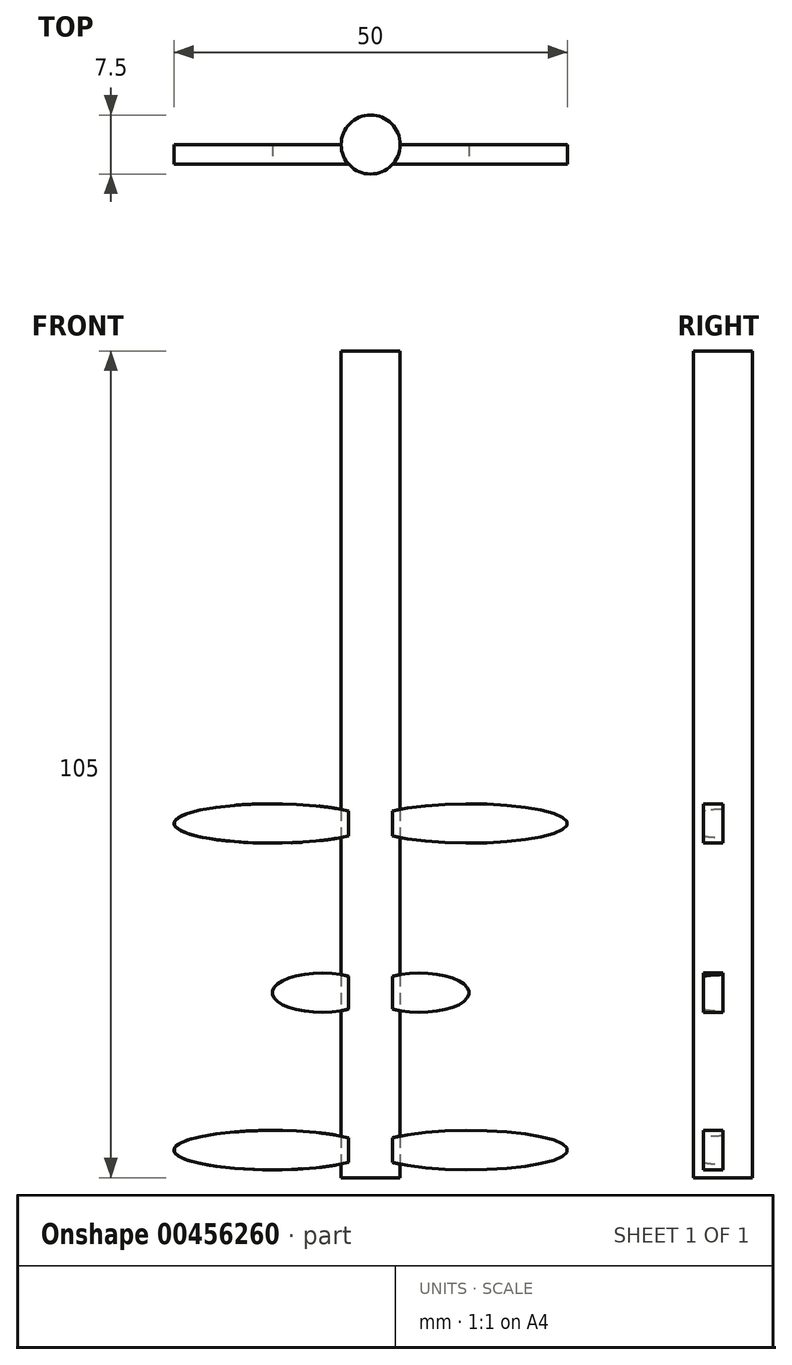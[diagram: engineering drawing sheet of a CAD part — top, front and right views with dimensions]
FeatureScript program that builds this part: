
annotation { "Feature Type Name" : "Feature", "Feature Type Description" : "" }
export const myFeature = defineFeature(function(context is Context, id is Id, definition is map)
    precondition{}
    {
        {
            var Q0;
            Q0=qCreatedBy(makeId("Top.planeOp"),FACE);
            var sketch = newSketch(context, id + "F0", { "sketchPlane" : qUnion([Q0])});
            skCircle(sketch, "E0", {"center": v(0, 0) * mm, "radius": 3.75 * mm});
            skSolve(sketch);
        }
        {
            var Q0;
            Q0 = qSketchRegion(id + "F0", true);
            extrude(context, id + "F1", {"entities" : qUnion([Q0]), "depth" : 105 * mm});
        }
        {
            var Q0;
            Q0=qCreatedBy(makeId("Front.planeOp"),FACE);
            var sketch = newSketch(context, id + "F2", { "sketchPlane" : qUnion([Q0])});
            skEllipse(sketch, "E1", {"center": v(12.5, 3.5) * mm, "majorRadius": 12.5 * mm, "minorRadius": 2.5 * mm, "majorAxis": v(-1, 0)});
            skEllipse(sketch, "E2", {"center": v(12.5, 45) * mm, "majorRadius": 12.5 * mm, "minorRadius": 2.5 * mm, "majorAxis": v(-1, 0)});
            skEllipse(sketch, "E3", {"center": v(-12.5, 45) * mm, "majorRadius": 12.5 * mm, "minorRadius": 2.5 * mm, "majorAxis": v(-1, 0)});
            skEllipse(sketch, "E4", {"center": v(-12.5, 3.5) * mm, "majorRadius": 12.5 * mm, "minorRadius": 2.5 * mm, "majorAxis": v(-1, 0)});
            skEllipse(sketch, "E5", {"center": v(6.25, 23.5) * mm, "majorRadius": 6.25 * mm, "minorRadius": 2.5 * mm, "majorAxis": v(-1, 0)});
            skEllipse(sketch, "E6", {"center": v(-6.25, 23.5) * mm, "majorRadius": 6.25 * mm, "minorRadius": 2.5 * mm, "majorAxis": v(-1, 0)});
            skSolve(sketch);
        }
        {
            var Q0;
            Q0=makeQuery(id+"F2.imprint","IMPRINT",FACE,{"disambiguationData":[TD([[makeQuery(id+"F2.imprint","IMPRINT",EDGE,{"derivedFrom":sQuery(id+"F2.wireOp",EDGE,"E4")}),1.0]])]});
            var Q1;
            Q1=makeQuery(id+"F2.imprint","IMPRINT",FACE,{"disambiguationData":[TD([[makeQuery(id+"F2.imprint","IMPRINT",EDGE,{"derivedFrom":sQuery(id+"F2.wireOp",EDGE,"E5")}),1.0]])]});
            var Q2;
            Q2=makeQuery(id+"F2.imprint","IMPRINT",FACE,{"disambiguationData":[TD([[makeQuery(id+"F2.imprint","IMPRINT",EDGE,{"derivedFrom":sQuery(id+"F2.wireOp",EDGE,"E6")}),1.0]])]});
            var Q3;
            Q3=makeQuery(id+"F2.imprint","IMPRINT",FACE,{"disambiguationData":[TD([[makeQuery(id+"F2.imprint","IMPRINT",EDGE,{"derivedFrom":sQuery(id+"F2.wireOp",EDGE,"E2")}),1.0]])]});
            var Q4;
            Q4=makeQuery(id+"F2.imprint","IMPRINT",FACE,{"disambiguationData":[TD([[makeQuery(id+"F2.imprint","IMPRINT",EDGE,{"derivedFrom":sQuery(id+"F2.wireOp",EDGE,"E3")}),1.0]])]});
            var Q5;
            Q5=makeQuery(id+"F2.imprint","IMPRINT",FACE,{"disambiguationData":[TD([[makeQuery(id+"F2.imprint","IMPRINT",EDGE,{"derivedFrom":sQuery(id+"F2.wireOp",EDGE,"E1")}),1.0]])]});
            extrude(context, id + "F3", {"entities" : qUnion([Q0, Q1, Q2, Q3, Q4, Q5]), "operationType" : NewBodyOperationType.ADD, "depth" : 2.5 * mm});
        }
    });
